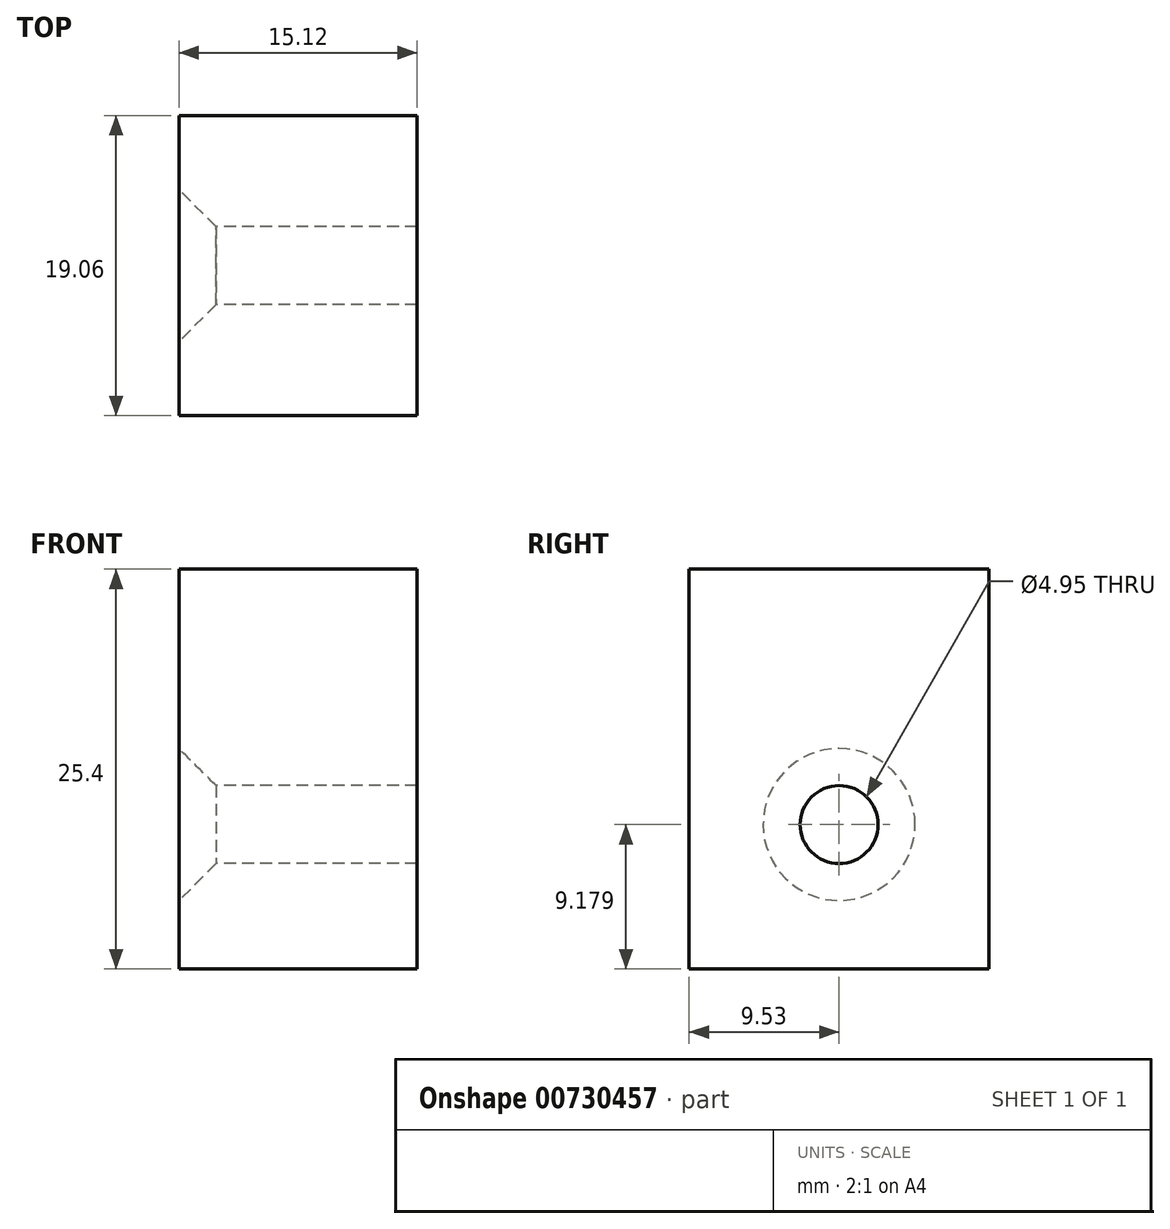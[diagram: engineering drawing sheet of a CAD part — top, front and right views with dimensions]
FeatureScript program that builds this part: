
annotation { "Feature Type Name" : "Feature", "Feature Type Description" : "" }
export const myFeature = defineFeature(function(context is Context, id is Id, definition is map)
    precondition{}
    {
        {
            var Q0;
            Q0=qCreatedBy(makeId("Top.planeOp"),FACE);
            var sketch = newSketch(context, id + "F0", { "sketchPlane" : qUnion([Q0])});
            skLineSegment(sketch, "E0.bottom", {"start": v(7.56, 9.53) * mm, "end": v(-7.56, 9.53) * mm});
            skLineSegment(sketch, "E0.top", {"start": v(7.56, -9.53) * mm, "end": v(-7.56, -9.53) * mm});
            skLineSegment(sketch, "E0.left", {"start": v(7.56, 9.53) * mm, "end": v(7.56, -9.53) * mm});
            skLineSegment(sketch, "E0.right", {"start": v(-7.56, 9.53) * mm, "end": v(-7.56, -9.53) * mm});
            skPoint(sketch, "E0.middle", {"position": v(0, 0) * mm});
            skLineSegment(sketch, "E1.bottom", {"start": v(7.56, 9.53) * mm, "end": v(-1.33, 9.53) * mm});
            skLineSegment(sketch, "E1.top", {"start": v(7.56, -9.53) * mm, "end": v(-1.33, -9.53) * mm});
            skLineSegment(sketch, "E1.right", {"start": v(-1.33, 9.53) * mm, "end": v(-1.33, -9.53) * mm});
            skSolve(sketch);
        }
        {
            var Q0;
            Q0=makeQuery(id+"F0.imprint","IMPRINT",FACE,{"disambiguationData":[TD([[makeQuery(id+"F0.imprint","IMPRINT",EDGE,{"derivedFrom":sQuery(id+"F0.wireOp",EDGE,"E0.bottom")}),1.0]])]});
            extrude(context, id + "F1", {"entities" : qUnion([Q0]), "depth" : 6.22 * mm, "offsetDistance" : 25.4 * mm, "hasSecondDirection" : true, "secondDirectionOppositeDirection" : true, "secondDirectionDepth" : 19.18 * mm});
        }
        {
            var Q0;
            Q0 = qSketchRegion(id + "F0", true);
            extrude(context, id + "F2", {"entities" : qUnion([Q0]), "operationType" : NewBodyOperationType.ADD, "oppositeDirection" : true, "depth" : 19.18 * mm, "offsetDistance" : 25.4 * mm});
        }
        {
            var Q0;
            Q0=qCreatedBy(makeId("Right.planeOp"),FACE);
            cPlane(context, id + "F3", {"entities" : qUnion([Q0]), "cplaneType" : CPlaneType.OFFSET, "offset" : 7.57 * mm, "oppositeDirection" : true, "width" : 152.4 * mm, "height" : 152.4 * mm});
        }
        {
            var Q0;
            Q0=qCreatedBy(id+"F3.planeOp",FACE);
            var sketch = newSketch(context, id + "F4", { "sketchPlane" : qUnion([Q0])});
            skPoint(sketch, "E2", {"position": v(0, -10) * mm});
            skSolve(sketch);
        }
        {
            var Q0;
            Q0=sQuery(id+"F4.wireOp",VERTEX,"E2");
            var Q1;
            Q1=makeQuery(id+"F1.opExtrude","SWEPT_BODY",BODY,{"disambiguationData":[OSD([sQuery(id+"F0.wireOp",EDGE,"E0.bottom"),sQuery(id+"F0.wireOp",EDGE,"E0.top"),sQuery(id+"F0.wireOp",EDGE,"E0.right"),sQuery(id+"F0.wireOp",EDGE,"E1.right")])]});
            hole(context, id + "F5", {"style" : HoleStyle.C_SINK, "endStyle" : HoleEndStyle.THROUGH, "oppositeDirection" : true, "holeDiameter" : 4.95 * mm, "cSinkDiameter" : 9.65 * mm, "cSinkAngle" : 90 * degree, "majorDiameter" : 6.35 * mm, "isTappedThrough" : true, "tappedDepth" : 12.7 * mm, "tapClearance" : 3, "locations" : qUnion([Q0]), "scope" : qUnion([Q1])});
        }
    });
